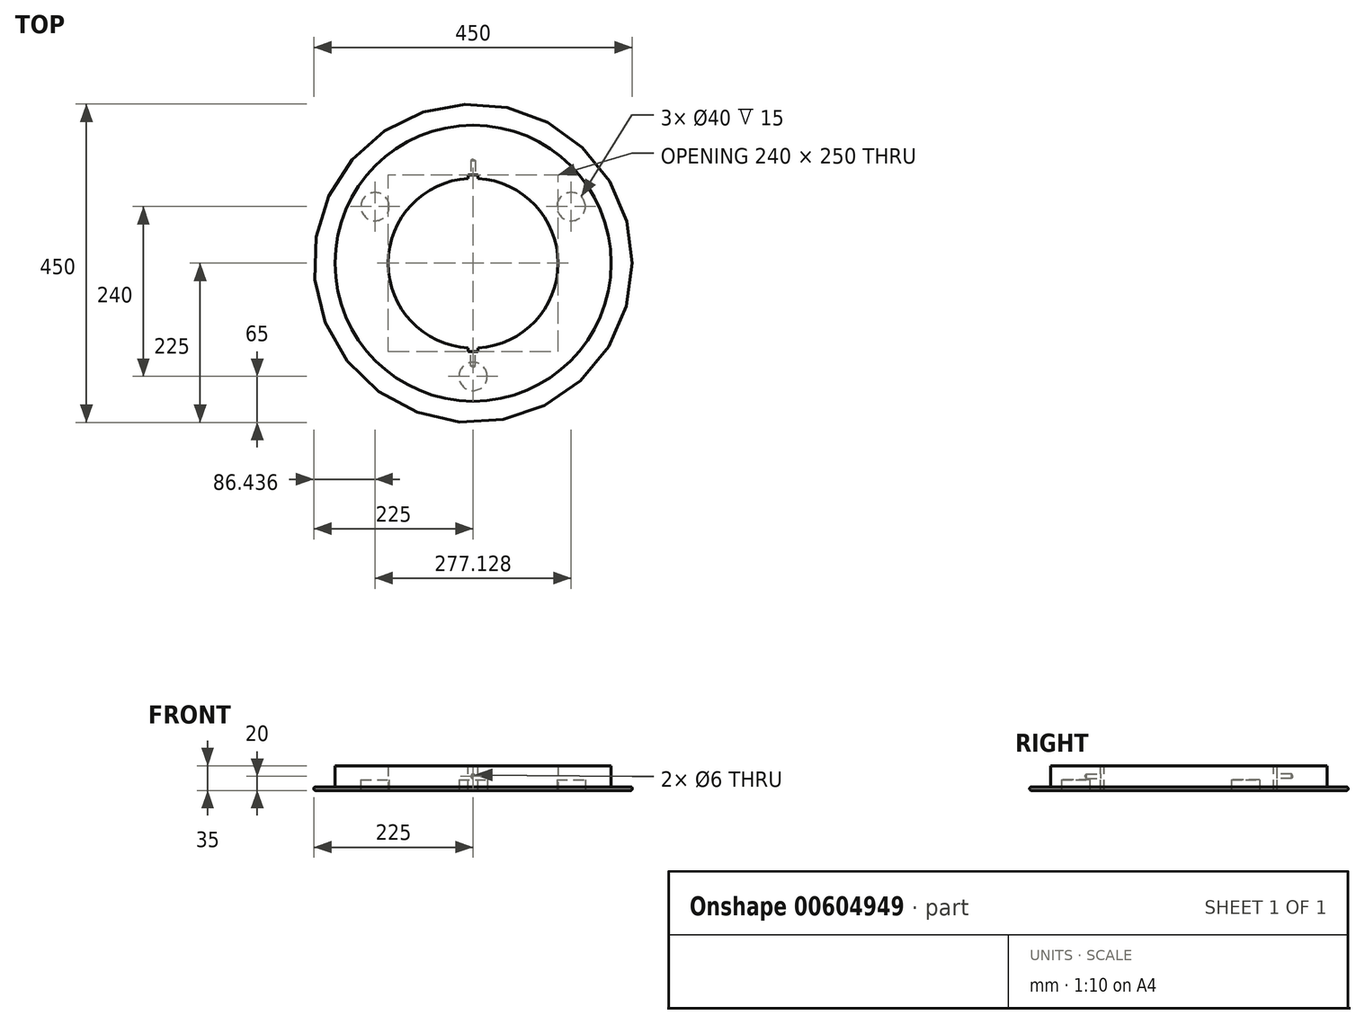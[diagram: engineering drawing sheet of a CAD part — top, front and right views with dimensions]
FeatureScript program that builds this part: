
annotation { "Feature Type Name" : "Feature", "Feature Type Description" : "" }
export const myFeature = defineFeature(function(context is Context, id is Id, definition is map)
    precondition{}
    {
        {
            var Q0;
            Q0=qCreatedBy(makeId("Top.planeOp"),FACE);
            var sketch = newSketch(context, id + "F0", { "sketchPlane" : qUnion([Q0])});
            skCircle(sketch, "E0", {"center": v(0, 0) * mm, "radius": 225 * mm});
            skCircle(sketch, "E1", {"center": v(0, 0) * mm, "radius": 120 * mm});
            skSolve(sketch);
        }
        {
            var Q0;
            Q0=makeQuery(id+"F0.imprint","IMPRINT",FACE,{"disambiguationData":[TD([[makeQuery(id+"F0.imprint","IMPRINT",EDGE,{"derivedFrom":sQuery(id+"F0.wireOp",EDGE,"E0")}),1.0]])]});
            extrude(context, id + "F1", {"entities" : qUnion([Q0]), "depth" : 5 * mm, "offsetDistance" : 25 * mm});
        }
        {
            var Q0;
            Q0=makeQuery(id+"F1.opExtrude","CAP_EDGE",EDGE,{"disambiguationData":[OSD([sQuery(id+"F0.wireOp",EDGE,"E0")])],"isStart":false});
            var Q1;
            Q1=makeQuery(id+"F1.opExtrude","CAP_EDGE",EDGE,{"disambiguationData":[OSD([sQuery(id+"F0.wireOp",EDGE,"E0")])],"isStart":true});
            fillet(context, id + "F2", {"entities" : qUnion([Q0, Q1]), "radius" : 2.5 * mm, "tangentPropagation" : true, "allowEdgeOverflow" : false});
        }
        {
            var Q0;
            Q0=makeQuery(id+"F1.opExtrude","CAP_FACE",FACE,{"disambiguationData":[OSD([sQuery(id+"F0.wireOp",EDGE,"E0"),sQuery(id+"F0.wireOp",EDGE,"E1")])],"isStart":false});
            var sketch = newSketch(context, id + "F3", { "sketchPlane" : qUnion([Q0])});
            skCircle(sketch, "E2", {"center": v(0, 0) * mm, "radius": 195 * mm});
            skCircle(sketch, "E3", {"center": v(0, 0) * mm, "radius": 120 * mm});
            skSolve(sketch);
        }
        {
            var Q0;
            Q0=makeQuery(id+"F3.imprint","IMPRINT",FACE,{"disambiguationData":[TD([[makeQuery(id+"F3.imprint","IMPRINT",EDGE,{"derivedFrom":sQuery(id+"F3.wireOp",EDGE,"E2")}),1.0]])]});
            extrude(context, id + "F4", {"entities" : qUnion([Q0]), "operationType" : NewBodyOperationType.ADD, "depth" : 30 * mm, "offsetDistance" : 25 * mm});
        }
        {
            var Q0;
            Q0=makeQuery(id+"F1.opExtrude","CAP_FACE",FACE,{"disambiguationData":[OSD([sQuery(id+"F0.wireOp",EDGE,"E0"),sQuery(id+"F0.wireOp",EDGE,"E1")])],"isStart":true});
            var sketch = newSketch(context, id + "F5", { "sketchPlane" : qUnion([Q0])});
            skLineSegment(sketch, "E4", {"start": v(0, 0) * mm, "end": v(0, 160) * mm});
            skCircle(sketch, "E5", {"center": v(0, 160) * mm, "radius": 20 * mm});
            skCircle(sketch, "E6.1.0", {"center": v(-138.56, -80) * mm, "radius": 20 * mm});
            skCircle(sketch, "E6.2.0", {"center": v(138.56, -80) * mm, "radius": 20 * mm});
            skPoint(sketch, "E6.center", {"position": v(0, 0) * mm});
            skSolve(sketch);
        }
        {
            var Q0;
            Q0=makeQuery(id+"F5.imprint","IMPRINT",FACE,{"disambiguationData":[TD([[makeQuery(id+"F5.imprint","IMPRINT",EDGE,{"derivedFrom":sQuery(id+"F5.wireOp",EDGE,"E5")}),1.0]])]});
            var Q1;
            Q1=makeQuery(id+"F5.imprint","IMPRINT",FACE,{"disambiguationData":[TD([[makeQuery(id+"F5.imprint","IMPRINT",EDGE,{"derivedFrom":sQuery(id+"F5.wireOp",EDGE,"E6.2.0")}),1.0]])]});
            var Q2;
            Q2=makeQuery(id+"F5.imprint","IMPRINT",FACE,{"disambiguationData":[TD([[makeQuery(id+"F5.imprint","IMPRINT",EDGE,{"derivedFrom":sQuery(id+"F5.wireOp",EDGE,"E6.1.0")}),1.0]])]});
            extrude(context, id + "F6", {"entities" : qUnion([Q0, Q1, Q2]), "operationType" : NewBodyOperationType.REMOVE, "oppositeDirection" : true, "depth" : 15 * mm, "offsetDistance" : 25 * mm});
        }
        {
            var Q0;
            Q0=makeQuery(id+"F4.opExtrude","CAP_FACE",FACE,{"disambiguationData":[OSD([sQuery(id+"F3.wireOp",EDGE,"E2"),sQuery(id+"F3.wireOp",EDGE,"E3")])],"isStart":false});
            var sketch = newSketch(context, id + "F7", { "sketchPlane" : qUnion([Q0])});
            skLineSegment(sketch, "E7", {"start": v(0, 0) * mm, "end": v(0, 120) * mm});
            skLineSegment(sketch, "E8", {"start": v(0, 120) * mm, "end": v(0, 125) * mm});
            skLineSegment(sketch, "E9", {"start": v(0, 125) * mm, "end": v(7, 125) * mm});
            skLineSegment(sketch, "E10", {"start": v(7, 125) * mm, "end": v(7, 119.8) * mm});
            skLineSegment(sketch, "E11", {"start": v(0, 125) * mm, "end": v(-7, 125) * mm});
            skLineSegment(sketch, "E12", {"start": v(-7, 125) * mm, "end": v(-7, 119.8) * mm});
            skLineSegment(sketch, "E13", {"start": v(0, 0) * mm, "end": v(24.44, 0) * mm});
            skLineSegment(sketch, "E14.MirrorCS", {"start": v(0, -120) * mm, "end": v(0, -125) * mm});
            skLineSegment(sketch, "E15.MirrorCS", {"start": v(0, -125) * mm, "end": v(7, -125) * mm});
            skLineSegment(sketch, "E16.MirrorCS", {"start": v(7, -125) * mm, "end": v(7, -119.8) * mm});
            skLineSegment(sketch, "E17.MirrorCS", {"start": v(-7, -125) * mm, "end": v(-7, -119.8) * mm});
            skLineSegment(sketch, "E18.MirrorCS", {"start": v(0, -125) * mm, "end": v(-7, -125) * mm});
            skSolve(sketch);
        }
        {
            var Q0;
            {var subQ0=sQuery(id+"F7.wireOp",EDGE,"E8");Q0=makeQuery(id+"F7.imprint","IMPRINT",FACE,{"disambiguationData":[TD([[makeQuery(id+"F7.imprint","IMPRINT",EDGE,{"derivedFrom":subQ0}),-1.0]])]});}
            var Q1;
            {var subQ0=sQuery(id+"F7.wireOp",EDGE,"E8");Q1=makeQuery(id+"F7.imprint","IMPRINT",FACE,{"disambiguationData":[TD([[makeQuery(id+"F7.imprint","IMPRINT",EDGE,{"derivedFrom":subQ0}),1.0]])]});}
            var Q2;
            {var subQ0=sQuery(id+"F7.wireOp",EDGE,"E14.MirrorCS");Q2=makeQuery(id+"F7.imprint","IMPRINT",FACE,{"disambiguationData":[TD([[makeQuery(id+"F7.imprint","IMPRINT",EDGE,{"derivedFrom":subQ0}),1.0]])]});}
            var Q3;
            {var subQ0=sQuery(id+"F7.wireOp",EDGE,"E14.MirrorCS");Q3=makeQuery(id+"F7.imprint","IMPRINT",FACE,{"disambiguationData":[TD([[makeQuery(id+"F7.imprint","IMPRINT",EDGE,{"derivedFrom":subQ0}),-1.0]])]});}
            extrude(context, id + "F8", {"entities" : qUnion([Q0, Q1, Q2, Q3]), "operationType" : NewBodyOperationType.REMOVE, "endBound" : BoundingType.THROUGH_ALL, "oppositeDirection" : true, "depth" : 25 * mm, "offsetDistance" : 25 * mm});
        }
        {
            var Q0;
            Q0=makeQuery(id+"F8.boolean.opBoolean","COPY",FACE,{"derivedFrom":makeQuery(id+"F8.opExtrude","SWEPT_FACE",FACE,{"disambiguationData":[OSD([sQuery(id+"F7.wireOp",EDGE,"E15.MirrorCS"),sQuery(id+"F7.wireOp",EDGE,"E18.MirrorCS")])]})});
            var sketch = newSketch(context, id + "F9", { "sketchPlane" : qUnion([Q0])});
            skPoint(sketch, "E19", {"position": v(0, 20) * mm});
            skSolve(sketch);
        }
        {
            var Q0;
            Q0=sQuery(id+"F9.wireOp",VERTEX,"E19");
            var Q1;
            Q1=sQuery(id+"F9.wireOp",VERTEX,"4183395d-7ad4-4854-adf9-82fd268e4799");
            var Q2;
            Q2=makeQuery(id+"F1.opExtrude","SWEPT_BODY",BODY,{"disambiguationData":[OSD([sQuery(id+"F0.wireOp",EDGE,"E0"),sQuery(id+"F0.wireOp",EDGE,"E1")])]});
            hole(context, id + "F10", {"style" : HoleStyle.SIMPLE, "endStyle" : HoleEndStyle.BLIND, "holeDiameter" : 6 * mm, "majorDiameter" : 5 * mm, "holeDepth" : 20 * mm, "isTappedThrough" : true, "tappedDepth" : 12 * mm, "tapClearance" : 3, "locations" : qUnion([Q0, Q1]), "scope" : qUnion([Q2])});
        }
        {
            var Q0;
            Q0=makeQuery(id+"F8.boolean.opBoolean","COPY",FACE,{"derivedFrom":makeQuery(id+"F8.opExtrude","SWEPT_FACE",FACE,{"disambiguationData":[OSD([sQuery(id+"F7.wireOp",EDGE,"E9"),sQuery(id+"F7.wireOp",EDGE,"E11")])]})});
            var sketch = newSketch(context, id + "F11", { "sketchPlane" : qUnion([Q0])});
            skPoint(sketch, "E20", {"position": v(0, 20) * mm});
            skPoint(sketch, "E20.positionSnap0", {"position": v(0, 35) * mm});
            skSolve(sketch);
        }
        {
            var Q0;
            Q0=sQuery(id+"F11.wireOp",VERTEX,"E20");
            var Q1;
            Q1=makeQuery(id+"F1.opExtrude","SWEPT_BODY",BODY,{"disambiguationData":[OSD([sQuery(id+"F0.wireOp",EDGE,"E0"),sQuery(id+"F0.wireOp",EDGE,"E1")])]});
            hole(context, id + "F12", {"style" : HoleStyle.SIMPLE, "endStyle" : HoleEndStyle.BLIND, "holeDiameter" : 6 * mm, "majorDiameter" : 5 * mm, "holeDepth" : 20 * mm, "isTappedThrough" : true, "tappedDepth" : 12 * mm, "tapClearance" : 3, "locations" : qUnion([Q0]), "scope" : qUnion([Q1])});
        }
    });
